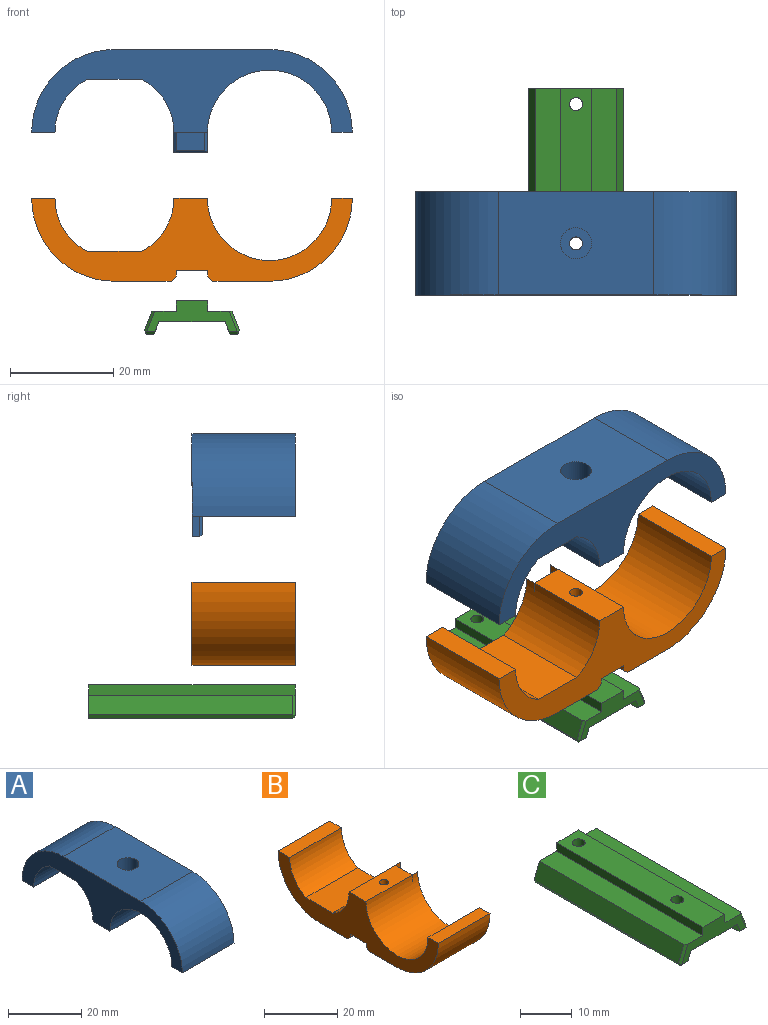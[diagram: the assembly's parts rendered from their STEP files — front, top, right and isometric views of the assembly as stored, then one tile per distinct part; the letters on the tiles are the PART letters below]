
ASSEMBLY  parts=3 mates=2
PART A: 22 faces, bbox 20x62x20 mm
  f0: plane 18.5x6.5mm, normal (0,0,-1), area 112.3mm2, adj f1,f2,f10,f12,f18,f19,f21
  f1: cylinder r=1.25mm len=11mm, axis (0,0,-1), area 86.4mm2, adj f0,f13
  f2: cylinder r=11.5mm len=20mm, axis (-1,0,0), area 253mm2, adj f0,f3,f11,f12,f15
  f3: plane 20x10.43mm, normal (0,0,-1), area 208.6mm2, adj f2,f4,f11,f12
  f4: cylinder r=11.5mm len=20mm, axis (-1,0,0), area 253mm2, adj f3,f5,f11,f12
  f5: plane 20x4.5mm, normal (0,0,-1), area 90mm2, adj f4,f6,f11,f12
  f6: cylinder r=16mm len=20mm, axis (-1,0,0), area 502.7mm2, adj f5,f7,f11,f12
  f7: plane 30x20mm, normal (0,0,1), area 571.7mm2, adj f6,f8,f11,f12,f14
  f8: cylinder r=16mm len=20mm, axis (-1,0,0), area 502.7mm2, adj f7,f9,f11,f12
  f9: plane 20x4mm, normal (0,0,-1), area 80mm2, adj f8,f10,f11,f12
  f10: cylinder r=12mm len=24mm, axis (-1,0,0), area 754mm2, adj f0,f9,f11,f12,f16
  f11: plane 62x20mm, normal (1,0,0), area 483mm2, adj f2,f3,f4,f5,f6,f7,f8,f9
  f12: plane 62x16mm, normal (-1,0,0), area 457mm2, adj f0,f2,f3,f4,f5,f6,f7,f8
  f13: plane 6x6mm, normal (0,0,1), area 23.4mm2, adj f1,f14
  f14: cylinder r=3mm len=6mm, axis (0,0,1), area 94.2mm2, adj f7,f13
  f15: plane 4x1.5mm, normal (0,1,0), area 6mm2, adj f2,f11,f17,f21
  f16: plane 4x1.5mm, normal (0,-1,0), area 6mm2, adj f10,f11,f17,f19
  f17: plane 6.5x1.5mm, normal (0,0,-1), area 9.7mm2, adj f11,f15,f16,f20
  f18: plane 5.5x3.5mm, normal (-1,0,0), area 19.3mm2, adj f0,f19,f20,f21
  f19: plane 4x0.5mm, normal (-0.71,-0.71,0), area 2.7mm2, adj f0,f16,f18,f20
  f20: plane 6.5x0.5mm, normal (-0.71,0,-0.71), area 4.2mm2, adj f17,f18,f19,f21
  f21: plane 4x0.5mm, normal (-0.71,0.71,0), area 2.7mm2, adj f0,f15,f18,f20
PART B: 23 faces, bbox 20x62x16 mm
  f0: plane 17.9x6.5mm, normal (0,0,1), area 111.4mm2, adj f2,f14,f15,f18,f22
  f1: plane 62x16mm, normal (1,0,0), area 416.5mm2, adj f2,f3,f4,f5,f6,f7,f8,f9
  f2: cylinder r=12mm len=24mm, axis (-1,0,0), area 754mm2, adj f0,f1,f3,f15,f20
  f3: plane 20x4mm, normal (0,0,1), area 80mm2, adj f1,f2,f4,f15
  f4: cylinder r=16mm len=20mm, axis (-1,0,0), area 502.7mm2, adj f1,f3,f5,f15
  f5: plane 20x10.95mm, normal (0,0,-1), area 219mm2, adj f1,f4,f15,f17
  f6: plane 20x1.1mm, normal (0,1,0), area 22mm2, adj f1,f7,f15,f17
  f7: plane 20x6.1mm, normal (0,0,-1), area 117.1mm2, adj f1,f6,f8,f15,f18
  f8: plane 20x1.1mm, normal (0,-1,0), area 22mm2, adj f1,f7,f15,f16
  f9: plane 20x10.95mm, normal (0,0,-1), area 219mm2, adj f1,f10,f15,f16
  f10: cylinder r=16mm len=20mm, axis (-1,0,0), area 502.7mm2, adj f1,f9,f11,f15
  f11: plane 20x4.5mm, normal (0,0,1), area 90mm2, adj f1,f10,f12,f15
  f12: cylinder r=11.5mm len=20mm, axis (-1,0,0), area 253mm2, adj f1,f11,f13,f15
  f13: plane 20x10.43mm, normal (0,0,1), area 208.6mm2, adj f1,f12,f14,f15
  f14: cylinder r=11.5mm len=20mm, axis (-1,0,0), area 253mm2, adj f0,f1,f13,f15,f19
  f15: plane 62x16mm, normal (-1,0,0), area 443.2mm2, adj f0,f2,f3,f4,f5,f6,f7,f8
  f16: plane 20x1mm, normal (0,-0.71,-0.71), area 28.3mm2, adj f1,f8,f9,f15
  f17: plane 20x1mm, normal (0,0.71,-0.71), area 28.3mm2, adj f1,f5,f6,f15
  f18: cylinder r=1.25mm len=13.9mm, axis (0,0,-1), area 109.2mm2, adj f0,f7
  f19: plane 4.1x2.1mm, normal (0,-1,0), area 8.6mm2, adj f1,f14,f21,f22
  f20: plane 4.1x2.1mm, normal (0,1,0), area 8.6mm2, adj f1,f2,f21,f22
  f21: plane 6.5x2.1mm, normal (0,0,1), area 13.6mm2, adj f1,f19,f20,f22
  f22: plane 6.5x4.1mm, normal (1,0,0), area 26.7mm2, adj f0,f19,f20,f21
PART C: 24 faces, bbox 18.5x40x6.5 mm
  f0: plane 40x4.75mm, normal (0,0,1), area 189.9mm2, adj f1,f11,f12,f13,f17
  f1: plane 39.5x3.82mm, normal (-0.93,0,0.36), area 161.8mm2, adj f0,f13,f16,f17
  f2: plane 39.5x1.42mm, normal (0,0,-1), area 55.9mm2, adj f3,f13,f16,f19
  f3: plane 40x2.5mm, normal (0.93,0,-0.36), area 107.2mm2, adj f2,f4,f12,f13,f19
  f4: plane 40x12.76mm, normal (0,0,-1), area 500.7mm2, adj f3,f5,f12,f13,f14,f15
  f5: plane 40x2.5mm, normal (-0.93,0,-0.36), area 107.2mm2, adj f4,f6,f12,f13,f23
  f6: plane 39.5x1.42mm, normal (0,0,-1), area 55.9mm2, adj f5,f13,f21,f23
  f7: plane 39.5x3.82mm, normal (0.93,0,0.36), area 161.8mm2, adj f8,f13,f20,f21
  f8: plane 40x4.75mm, normal (0,0,1), area 189.9mm2, adj f7,f9,f12,f13,f20
  f9: plane 40x2mm, normal (1,0,0), area 80mm2, adj f8,f10,f12,f13
  f10: plane 40x6mm, normal (0,0,1), area 230.2mm2, adj f9,f11,f12,f13,f14,f15
  f11: plane 40x2mm, normal (-1,0,0), area 80mm2, adj f0,f10,f12,f13
  f12: plane 17.54x6mm, normal (0,-1,0), area 48.8mm2, adj f0,f3,f4,f5,f8,f9,f10,f11
  f13: plane 18.47x6.5mm, normal (0,1,0), area 54.8mm2, adj f0,f1,f2,f3,f4,f5,f6,f7
  f14: cylinder r=1.25mm len=4mm, axis (0,0,1), area 31.4mm2, adj f4,f10
  f15: cylinder r=1.25mm len=4mm, axis (0,0,1), area 31.4mm2, adj f4,f10
  f16: plane 39.5x0.68mm, normal (-0.83,0,-0.56), area 32.6mm2, adj f1,f2,f13,f18
  f17: plane 4x2.02mm, normal (-0.66,-0.71,0.26), area 3mm2, adj f0,f1,f12,f18
  f18: plane 0.68x0.5mm, normal (-0.72,-0.49,-0.49), area 0.2mm2, adj f16,f17,f19
  f19: plane 1.61x0.5mm, normal (0,-0.71,-0.71), area 1.1mm2, adj f2,f3,f12,f18
  f20: plane 4x2.02mm, normal (0.66,-0.71,0.26), area 3mm2, adj f7,f8,f12,f22
  f21: plane 39.5x0.68mm, normal (0.83,0,-0.56), area 32.6mm2, adj f6,f7,f13,f22
  f22: plane 0.68x0.5mm, normal (0.72,-0.49,-0.49), area 0.2mm2, adj f20,f21,f23
  f23: plane 1.61x0.5mm, normal (0,-0.71,-0.71), area 1.1mm2, adj f5,f6,f12,f22
PLACE A rot(axis=(0,0,1),90deg) t=(-7.75,-28.32,37.82)mm
PLACE B rot(axis=(0,0,1),90deg) t=(-7.75,-28.32,25.02)mm
PLACE C t=(-7.75,1.68,15.22)mm
MATE slider B.f18 <-> C.f14  axis (0,0,-1) through (-7.75,-28.32,23.12)mm
MATE slider B.f18 <-> A.f1  axis (0,0,1) through (-7.75,-28.32,37.02)mm
